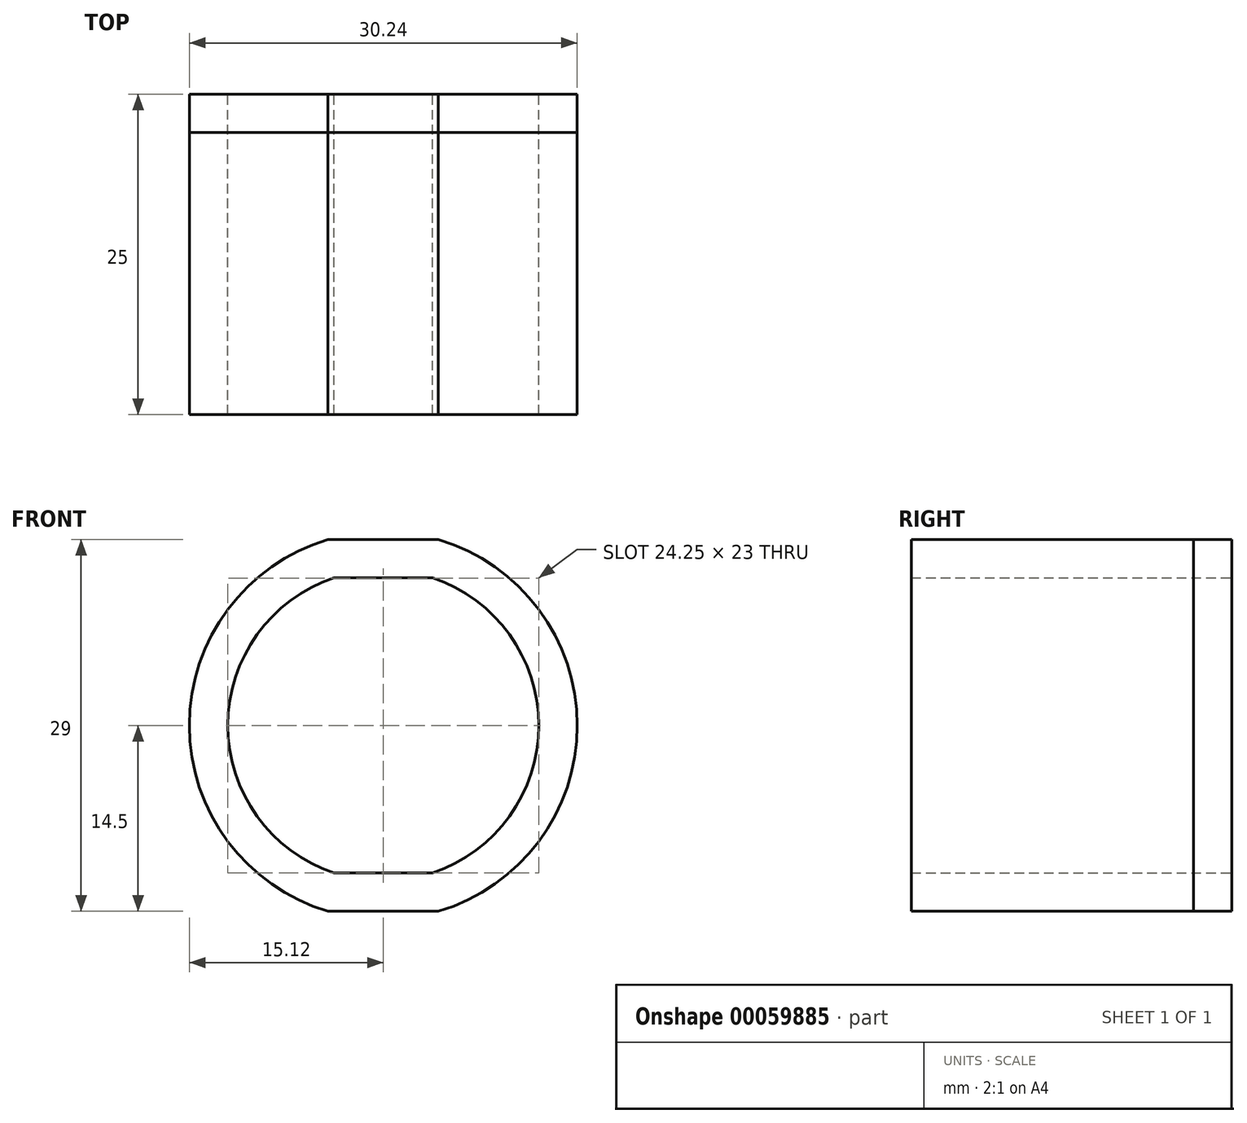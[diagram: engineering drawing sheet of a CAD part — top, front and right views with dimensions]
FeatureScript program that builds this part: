
annotation { "Feature Type Name" : "Feature", "Feature Type Description" : "" }
export const myFeature = defineFeature(function(context is Context, id is Id, definition is map)
    precondition{}
    {
        {
            var Q0;
            Q0=qCreatedBy(makeId("Front.planeOp"),FACE);
            var sketch = newSketch(context, id + "F0", { "sketchPlane" : qUnion([Q0])});
            skArc(sketch, "E0", {"start": v(-3.84, 11.5) * mm, "mid": v(-12.12, 0) * mm, "end": v(-3.84, -11.5) * mm});
            skLineSegment(sketch, "E1", {"start": v(-21.62, 0) * mm, "end": v(25.9, 0) * mm, "construction": true});
            skLineSegment(sketch, "E2.0", {"start": v(-3.84, -11.5) * mm, "end": v(3.84, -11.5) * mm});
            skLineSegment(sketch, "E3.0", {"start": v(-3.84, 11.5) * mm, "end": v(3.84, 11.5) * mm});
            skArc(sketch, "E4.trimOffspring", {"start": v(3.84, -11.5) * mm, "mid": v(12.12, 0) * mm, "end": v(3.84, 11.5) * mm});
            skLineSegment(sketch, "E5.0", {"start": v(-4.3, -14.5) * mm, "end": v(4.3, -14.5) * mm});
            skArc(sketch, "E5.1", {"start": v(-4.3, 14.5) * mm, "mid": v(-15.12, 0) * mm, "end": v(-4.3, -14.5) * mm});
            skLineSegment(sketch, "E5.2", {"start": v(-4.3, 14.5) * mm, "end": v(4.3, 14.5) * mm});
            skArc(sketch, "E5.3", {"start": v(4.3, -14.5) * mm, "mid": v(15.12, 0) * mm, "end": v(4.3, 14.5) * mm});
            skSolve(sketch);
        }
        {
            var Q0;
            Q0=makeQuery(id+"F0.imprint","IMPRINT",FACE,{"disambiguationData":[TD([[makeQuery(id+"F0.imprint","IMPRINT",EDGE,{"derivedFrom":sQuery(id+"F0.wireOp",EDGE,"E0")}),1.0]])]});
            var Q1;
            Q1=makeQuery(id+"F0.imprint","IMPRINT",FACE,{"disambiguationData":[TD([[makeQuery(id+"F0.imprint","IMPRINT",EDGE,{"derivedFrom":sQuery(id+"F0.wireOp",EDGE,"E0")}),-1.0]])]});
            extrude(context, id + "F1", {"entities" : qUnion([Q0, Q1]), "depth" : 3 * mm});
        }
        {
            var Q0;
            Q0=makeQuery(id+"F0.imprint","IMPRINT",FACE,{"disambiguationData":[TD([[makeQuery(id+"F0.imprint","IMPRINT",EDGE,{"derivedFrom":sQuery(id+"F0.wireOp",EDGE,"E0")}),-1.0]])]});
            extrude(context, id + "F2", {"entities" : qUnion([Q0]), "depth" : 25 * mm});
        }
    });
